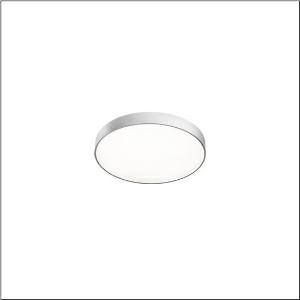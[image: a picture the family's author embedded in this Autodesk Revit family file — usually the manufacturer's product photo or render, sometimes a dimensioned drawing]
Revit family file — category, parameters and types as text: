
# Revit family: round_21_s_51mr34gd0421s
name_source: partatom
category: Lighting Fixtures
units: mm (PartAtom-declared; Revit-internal decimal feet)

## family parameters
Cut with Voids When Loaded = No
Host = Face
Light Source = No
Part Type = Normal
Room Calculation Point = No
Round Connector Dimension = Use Diameter
Shared = No

## types (1)
- Round 21 S (1 x LED, 3490 lm, 28 W, 4000K)
    Apparent Load = 28 VA
    CIE Flux Codes = 49 80 96 79 100
    Color Rendering = 80
    Color Temperature = 4000K
    Default Elevation = 1800 mm
    Description = Round 21 S, wall and ceiling luminaire, primary optical cover: cover, of PMMA, opal, light emission: direct/indirect distribution, primary light characteristic: symmetric, installation type: suspended mounting, surface-mounted, LED, rated luminous flux: 3.580lm, luminous efficacy: 118lm/W, light colour: 840, colour temperature: 4000K, with terminal, 5-pole, mains connection: 230V, AC, 50/60Hz, rated input power: 30W, housing, of aluminium, coated, silver, diameter: 400mm, height: 62mm, protection rating (complete): IP40, insulation class (complete): insulation class I (protective earthing), certification: CE, impact resistance: IK04, permissible operating ambient temperature: -10..+35°C, packaging unit: 1 piece
    Height = 87 mm
    Lamp = 1 x LED
    Lamp Light Flux = 3490 lm
    Lamp Power = 28 W
    Lamp count = 1
    Length = 400 mm
    Luminous efficacy = 125 lm/W
    Manufacturer = Siteco
    ModVariant = No
    Model = 51MR34GD0421S
    Mounting Place = Ceiling
    Mounting Type = Surface mounted
    Number of Poles = 1
    OnlyDefault = Yes
    Power Factor = 1
    Product Name = Round 21 S
    Product group = wall and ceiling luminaire
    ProductGroupID = 302
    Protection Class = Protection class I
    Protection Degree = IP 40
    RLX_Detail_Level = 1
    RLX_Emergency_Light_Flux = 0 lm
    RLX_Emergency_Type = 0
    RLX_Emergency_Type_DB = No
    RlxData = <blob elided: 11521 chars, md5=1919aa84>
    Socket = socket
    Standby Power = 0 W
    System Light Flux = 3490 lm
    System Power = 28 W
    Type Comments = Product without accessories
    Type Image = l_1258309.jpg
    URL = http://relux.com
    VarID = ---
    Voltage = 0 V
    Weight = 0.00 kg
    Width = 0 mm  [stored 0 ft]

note: [stored X ft] marks values corroborated as IEEE doubles in the binary element streams (Revit-internal decimal feet)

## geometry (parser evidence)
native form markers: Sweep x13
no freeform markers — native parametric forms only
